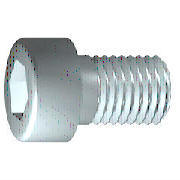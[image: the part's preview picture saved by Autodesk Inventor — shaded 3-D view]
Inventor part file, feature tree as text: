
AUTODESK INVENTOR PART (.ipt)
format: ipt  version: 2023.3 (Build 273359000, 359)  size: 186,880 bytes
history: native  units: mm (DEFAULTED — no unit token found)
features: sketch x2, other x1, extrude x1, plane x1, fillet x1
ambient origin geometry x7: Origin, YZ Plane, XY Plane, X Axis, Y Axis, Z Axis, Center Point
bodies: Solid1 (feature_tree)
feature tree (6):
  other  "Körper"
  extrude  "Loch"  Depth=2.0mm
  plane  "Work Plane1"
  fillet  "Fillet2"  Radius=2.0mm
  sketch  "Skizze1"  dims[d1=15.0mm d2=0.24548mm d3=2.0mm]
  sketch  "Skizze2"  dims[d4=1.0mm d5=60.0deg d6=2.0mm d7=2.0mm d8=1.732051mm d9=3.8mm d10=90.0deg d11=10.0mm d12=0.0mm d13=15.0mm d14=0.0mm d15=0.24538mm d16=0.24538mm d17=0.2mm d19=0.0mm d26=16.0mm d27=45.0deg d28=0.0mm d29=0.0mm d30=0.1mm]
